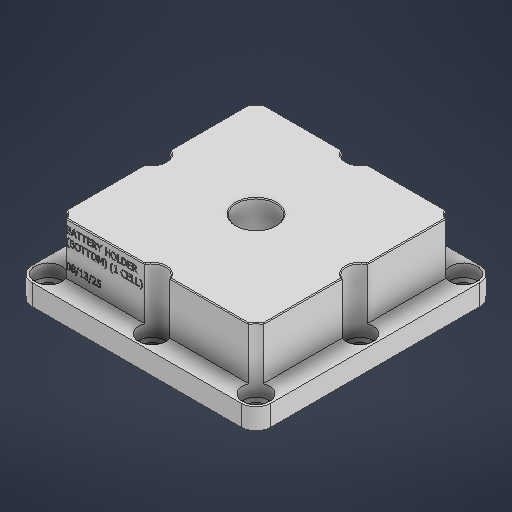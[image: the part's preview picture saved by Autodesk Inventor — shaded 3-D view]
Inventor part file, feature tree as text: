
AUTODESK INVENTOR PART (.ipt)
format: ipt  version: 2025 (Build 290162000, 162)  size: 902,656 bytes
history: native  units: in
note: dims shown in document units (in); Inventor stores cm internally (conversion verified against a paired STEP export)
features: sketch x5, extrude x3, hole x1, fillet x1, chamfer x1
ambient origin geometry x8: Origin, YZ Plane, XZ Plane, XY Plane, X Axis, Y Axis, Z Axis, Center Point
bodies: Solid1 (feature_tree)
feature tree (11):
  extrude  "Extrusion1"  Depth=4.5276in
  extrude  "Extrusion2"  Depth=3.7402in
  hole  "Hole3"  [1 undecoded]
  fillet  "Fillet1"  Radius=3.937in
  chamfer  "Chamfer1"  Distance=1.1811in
  extrude  "Extrusion3"  Depth=0.2805in
  sketch  "Sketch1"  dims[d0=4.5276in d1=4.5276in]
  sketch  "Sketch4"  dims[d2=0.3937in d3=0.0in d48=3.7402in]
  sketch  "Sketch5"  dims[d49=3.7402in d57=0.9843in d58=0.0in d156=3.937in]
  sketch  "Sketch Rectangular Pattern13"  dims[d158=0.2756in d159=1.1811in d161=1.9685in d162=1.1811in d164=1.9685in d167=0.2805in d168=0.2362in d169=0.5118in d170=1.2205in d171=90.0deg d172=0.315in d173=0.8108in d174=0.2805in d175=0.0157in d176=0.0787in d177=45.0deg d178=0.0787in d179=0.0in d180=0.748in]
  sketch  "Sketch6"  dims[d157=3.937in]
note: 1 required parameter value undecoded (feature->parameter linkage not recoverable at this tier; creation-order binding heuristic only, values carry confidence <= 0.55)
